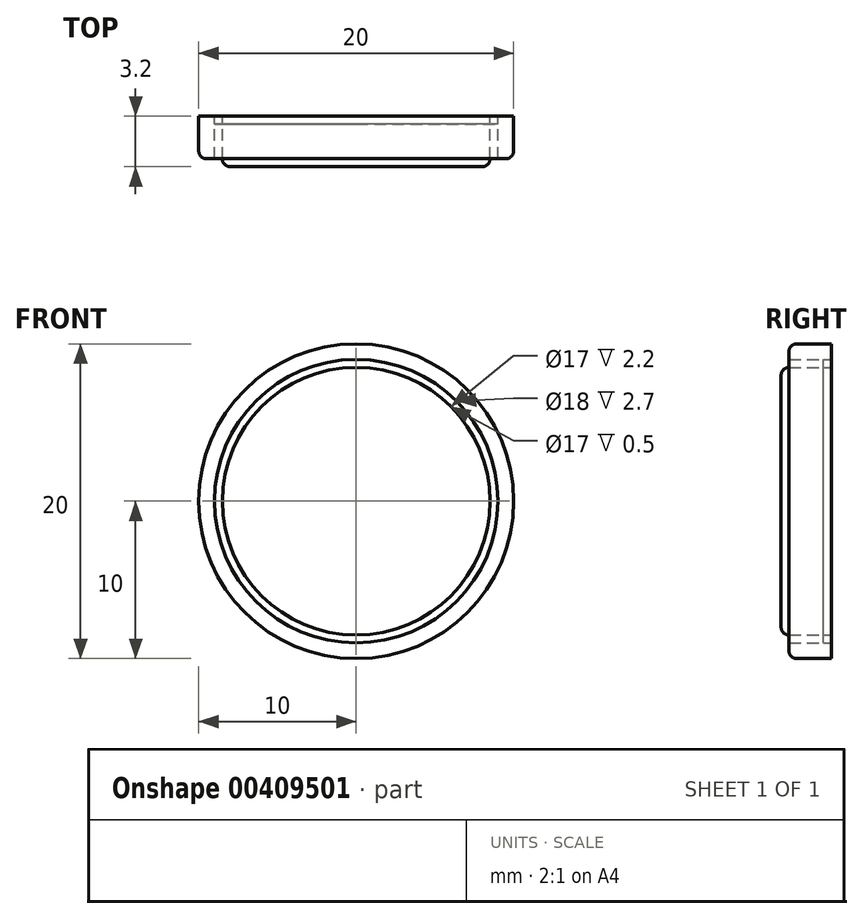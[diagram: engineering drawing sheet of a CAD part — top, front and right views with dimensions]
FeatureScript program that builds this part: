
annotation { "Feature Type Name" : "Feature", "Feature Type Description" : "" }
export const myFeature = defineFeature(function(context is Context, id is Id, definition is map)
    precondition{}
    {
        {
            var Q0;
            Q0=qCreatedBy(makeId("Front.planeOp"),FACE);
            var sketch = newSketch(context, id + "F0", { "sketchPlane" : qUnion([Q0]), "disableImprinting" : false});
            skCircle(sketch, "E0", {"center": v(0, 0) * mm, "radius": 10 * mm});
            skCircle(sketch, "E1", {"center": v(0, 0) * mm, "radius": 9 * mm});
            skCircle(sketch, "E2", {"center": v(0, 0) * mm, "radius": 8.5 * mm});
            skSolve(sketch);
        }
        {
            var Q0;
            Q0=makeQuery(id+"F0.imprint","IMPRINT",FACE,{"disambiguationData":[TD([[makeQuery(id+"F0.imprint","IMPRINT",EDGE,{"derivedFrom":sQuery(id+"F0.wireOp",EDGE,"E2")}),1.0]])]});
            var Q1;
            Q1=makeQuery(id+"F0.imprint","IMPRINT",FACE,{"disambiguationData":[TD([[makeQuery(id+"F0.imprint","IMPRINT",EDGE,{"derivedFrom":sQuery(id+"F0.wireOp",EDGE,"ab74bbfd-845b-4cb0-a3af-8f8529850c50.sketch_text.stroke-114")}),1.0]])]});
            var Q2;
            Q2=makeQuery(id+"F0.imprint","IMPRINT",FACE,{"disambiguationData":[TD([[makeQuery(id+"F0.imprint","IMPRINT",EDGE,{"derivedFrom":sQuery(id+"F0.wireOp",EDGE,"ab74bbfd-845b-4cb0-a3af-8f8529850c50.sketch_text.stroke-106")}),1.0]])]});
            var Q3;
            Q3=makeQuery(id+"F0.imprint","IMPRINT",FACE,{"disambiguationData":[TD([[makeQuery(id+"F0.imprint","IMPRINT",EDGE,{"derivedFrom":sQuery(id+"F0.wireOp",EDGE,"ab74bbfd-845b-4cb0-a3af-8f8529850c50.sketch_text.stroke-94")}),1.0]])]});
            var Q4;
            Q4=makeQuery(id+"F0.imprint","IMPRINT",FACE,{"disambiguationData":[TD([[makeQuery(id+"F0.imprint","IMPRINT",EDGE,{"derivedFrom":sQuery(id+"F0.wireOp",EDGE,"ab74bbfd-845b-4cb0-a3af-8f8529850c50.sketch_text.stroke-84")}),1.0]])]});
            var Q5;
            Q5=makeQuery(id+"F0.imprint","IMPRINT",FACE,{"disambiguationData":[TD([[makeQuery(id+"F0.imprint","IMPRINT",EDGE,{"derivedFrom":sQuery(id+"F0.wireOp",EDGE,"ab74bbfd-845b-4cb0-a3af-8f8529850c50.sketch_text.stroke-64")}),1.0]])]});
            var Q6;
            Q6=makeQuery(id+"F0.imprint","IMPRINT",FACE,{"disambiguationData":[TD([[makeQuery(id+"F0.imprint","IMPRINT",EDGE,{"derivedFrom":sQuery(id+"F0.wireOp",EDGE,"ab74bbfd-845b-4cb0-a3af-8f8529850c50.sketch_text.stroke-51")}),1.0]])]});
            var Q7;
            Q7=makeQuery(id+"F0.imprint","IMPRINT",FACE,{"disambiguationData":[TD([[makeQuery(id+"F0.imprint","IMPRINT",EDGE,{"derivedFrom":sQuery(id+"F0.wireOp",EDGE,"ab74bbfd-845b-4cb0-a3af-8f8529850c50.sketch_text.stroke-47")}),1.0]])]});
            var Q8;
            Q8=makeQuery(id+"F0.imprint","IMPRINT",FACE,{"disambiguationData":[TD([[makeQuery(id+"F0.imprint","IMPRINT",EDGE,{"derivedFrom":sQuery(id+"F0.wireOp",EDGE,"ab74bbfd-845b-4cb0-a3af-8f8529850c50.sketch_text.stroke-103")}),-1.0]])]});
            var Q9;
            Q9=makeQuery(id+"F0.imprint","IMPRINT",FACE,{"disambiguationData":[TD([[makeQuery(id+"F0.imprint","IMPRINT",EDGE,{"derivedFrom":sQuery(id+"F0.wireOp",EDGE,"ab74bbfd-845b-4cb0-a3af-8f8529850c50.sketch_text.stroke-43")}),1.0]])]});
            var Q10;
            Q10=makeQuery(id+"F0.imprint","IMPRINT",FACE,{"disambiguationData":[TD([[makeQuery(id+"F0.imprint","IMPRINT",EDGE,{"derivedFrom":sQuery(id+"F0.wireOp",EDGE,"ab74bbfd-845b-4cb0-a3af-8f8529850c50.sketch_text.stroke-30")}),1.0]])]});
            var Q11;
            Q11=makeQuery(id+"F0.imprint","IMPRINT",FACE,{"disambiguationData":[TD([[makeQuery(id+"F0.imprint","IMPRINT",EDGE,{"derivedFrom":sQuery(id+"F0.wireOp",EDGE,"ab74bbfd-845b-4cb0-a3af-8f8529850c50.sketch_text.stroke-14")}),1.0]])]});
            var Q12;
            Q12=makeQuery(id+"F0.imprint","IMPRINT",FACE,{"disambiguationData":[TD([[makeQuery(id+"F0.imprint","IMPRINT",EDGE,{"derivedFrom":sQuery(id+"F0.wireOp",EDGE,"ab74bbfd-845b-4cb0-a3af-8f8529850c50.sketch_text.stroke-6")}),1.0]])]});
            var Q13;
            Q13=makeQuery(id+"F0.imprint","IMPRINT",FACE,{"disambiguationData":[TD([[makeQuery(id+"F0.imprint","IMPRINT",EDGE,{"derivedFrom":sQuery(id+"F0.wireOp",EDGE,"ab74bbfd-845b-4cb0-a3af-8f8529850c50.sketch_text.stroke-10")}),1.0]])]});
            var Q14;
            Q14=makeQuery(id+"F0.imprint","IMPRINT",FACE,{"disambiguationData":[TD([[makeQuery(id+"F0.imprint","IMPRINT",EDGE,{"derivedFrom":sQuery(id+"F0.wireOp",EDGE,"ab74bbfd-845b-4cb0-a3af-8f8529850c50.sketch_text.stroke-0")}),1.0]])]});
            var Q15;
            Q15=makeQuery(id+"F0.imprint","IMPRINT",FACE,{"disambiguationData":[TD([[makeQuery(id+"F0.imprint","IMPRINT",EDGE,{"derivedFrom":sQuery(id+"F0.wireOp",EDGE,"ab74bbfd-845b-4cb0-a3af-8f8529850c50.sketch_text.stroke-183")}),1.0]])]});
            var Q16;
            Q16=makeQuery(id+"F0.imprint","IMPRINT",FACE,{"disambiguationData":[TD([[makeQuery(id+"F0.imprint","IMPRINT",EDGE,{"derivedFrom":sQuery(id+"F0.wireOp",EDGE,"ab74bbfd-845b-4cb0-a3af-8f8529850c50.sketch_text.stroke-167")}),1.0]])]});
            var Q17;
            Q17=makeQuery(id+"F0.imprint","IMPRINT",FACE,{"disambiguationData":[TD([[makeQuery(id+"F0.imprint","IMPRINT",EDGE,{"derivedFrom":sQuery(id+"F0.wireOp",EDGE,"ab74bbfd-845b-4cb0-a3af-8f8529850c50.sketch_text.stroke-159")}),1.0]])]});
            var Q18;
            Q18=makeQuery(id+"F0.imprint","IMPRINT",FACE,{"disambiguationData":[TD([[makeQuery(id+"F0.imprint","IMPRINT",EDGE,{"derivedFrom":sQuery(id+"F0.wireOp",EDGE,"ab74bbfd-845b-4cb0-a3af-8f8529850c50.sketch_text.stroke-163")}),-1.0]])]});
            var Q19;
            Q19=makeQuery(id+"F0.imprint","IMPRINT",FACE,{"disambiguationData":[TD([[makeQuery(id+"F0.imprint","IMPRINT",EDGE,{"derivedFrom":sQuery(id+"F0.wireOp",EDGE,"ab74bbfd-845b-4cb0-a3af-8f8529850c50.sketch_text.stroke-147")}),1.0]])]});
            var Q20;
            Q20=makeQuery(id+"F0.imprint","IMPRINT",FACE,{"disambiguationData":[TD([[makeQuery(id+"F0.imprint","IMPRINT",EDGE,{"derivedFrom":sQuery(id+"F0.wireOp",EDGE,"ab74bbfd-845b-4cb0-a3af-8f8529850c50.sketch_text.stroke-132")}),-1.0]])]});
            var Q21;
            Q21=makeQuery(id+"F0.imprint","IMPRINT",FACE,{"disambiguationData":[TD([[makeQuery(id+"F0.imprint","IMPRINT",EDGE,{"derivedFrom":sQuery(id+"F0.wireOp",EDGE,"ab74bbfd-845b-4cb0-a3af-8f8529850c50.sketch_text.stroke-132")}),1.0]])]});
            var Q22;
            Q22=makeQuery(id+"F0.imprint","IMPRINT",FACE,{"disambiguationData":[TD([[makeQuery(id+"F0.imprint","IMPRINT",EDGE,{"derivedFrom":sQuery(id+"F0.wireOp",EDGE,"ab74bbfd-845b-4cb0-a3af-8f8529850c50.sketch_text.stroke-122")}),1.0]])]});
            var Q23;
            Q23=makeQuery(id+"F0.imprint","IMPRINT",FACE,{"disambiguationData":[TD([[makeQuery(id+"F0.imprint","IMPRINT",EDGE,{"derivedFrom":sQuery(id+"F0.wireOp",EDGE,"ab74bbfd-845b-4cb0-a3af-8f8529850c50.sketch_text.stroke-211")}),1.0]])]});
            var Q24;
            Q24=makeQuery(id+"F0.imprint","IMPRINT",FACE,{"disambiguationData":[TD([[makeQuery(id+"F0.imprint","IMPRINT",EDGE,{"derivedFrom":sQuery(id+"F0.wireOp",EDGE,"ab74bbfd-845b-4cb0-a3af-8f8529850c50.sketch_text.stroke-195")}),1.0]])]});
            extrude(context, id + "F1", {"entities" : qUnion([Q0, Q1, Q2, Q3, Q4, Q5, Q6, Q7, Q8, Q9, Q10, Q11, Q12, Q13, Q14, Q15, Q16, Q17, Q18, Q19, Q20, Q21, Q22, Q23, Q24]), "depth" : 3.2 * mm});
        }
        {
            var Q0;
            Q0=makeQuery(id+"F0.imprint","IMPRINT",FACE,{"disambiguationData":[TD([[makeQuery(id+"F0.imprint","IMPRINT",EDGE,{"derivedFrom":sQuery(id+"F0.wireOp",EDGE,"E1")}),1.0]])]});
            extrude(context, id + "F2", {"entities" : qUnion([Q0]), "depth" : 2.2 * mm});
        }
        {
            var Q0;
            Q0=makeQuery(id+"F0.imprint","IMPRINT",FACE,{"disambiguationData":[TD([[makeQuery(id+"F0.imprint","IMPRINT",EDGE,{"derivedFrom":sQuery(id+"F0.wireOp",EDGE,"E0")}),1.0]])]});
            extrude(context, id + "F3", {"entities" : qUnion([Q0]), "depth" : 2.7 * mm});
        }
        {
            var Q0;
            Q0=makeQuery(id+"F3.opExtrude","CAP_EDGE",EDGE,{"disambiguationData":[OSD([sQuery(id+"F0.wireOp",EDGE,"E0")])],"isStart":false});
            fillet(context, id + "F4", {"entities" : qUnion([Q0]), "radius" : 0.5 * mm, "tangentPropagation" : true, "allowEdgeOverflow" : false});
        }
        {
            var Q0;
            Q0=makeQuery(id+"F1.opExtrude","CAP_EDGE",EDGE,{"disambiguationData":[OSD([sQuery(id+"F0.wireOp",EDGE,"E2")])],"isStart":false});
            fillet(context, id + "F5", {"entities" : qUnion([Q0]), "radius" : 0.5 * mm, "tangentPropagation" : true, "allowEdgeOverflow" : false});
        }
        {
            var Q0;
            Q0=makeQuery(id+"F2.opExtrude","SWEPT_BODY",BODY,{"disambiguationData":[OSD([sQuery(id+"F0.wireOp",EDGE,"E1"),sQuery(id+"F0.wireOp",EDGE,"E2")])]});
            transform(context, id + "F6", {"entities" : qUnion([Q0]), "transformType" : TransformType.TRANSLATION_3D, "dx" : 0 * mm, "dy" : -0.5 * mm, "dz" : 0 * mm, "makeCopy" : false});
        }
        {
            var Q0;
            Q0=makeQuery(id+"F3.opExtrude","CAP_FACE",FACE,{"disambiguationData":[OSD([sQuery(id+"F0.wireOp",EDGE,"E0"),sQuery(id+"F0.wireOp",EDGE,"E1")])],"isStart":false});
            extrude(context, id + "F7", {"entities" : qUnion([Q0]), "depth" : 0.5 * mm});
        }
        {
            var Q0;
            Q0=makeQuery(id+"F7.opExtrude","SWEPT_BODY",BODY,{"disambiguationData":[OSD([sQuery(id+"F0.wireOp",EDGE,"E0"),sQuery(id+"F0.wireOp",EDGE,"E1")])]});
            deleteBodies(context, id + "F8", {"entities" : qUnion([Q0])});
        }
        {
            var Q0;
            Q0=makeQuery(id+"F0.imprint","IMPRINT",FACE,{"disambiguationData":[TD([[makeQuery(id+"F0.imprint","IMPRINT",EDGE,{"derivedFrom":sQuery(id+"F0.wireOp",EDGE,"E1")}),1.0]])]});
            var Q1;
            Q1=sQuery(id+"F0.wireOp",EDGE,"E1");
            extrude(context, id + "F9", {"entities" : qUnion([Q0]), "surfaceEntities" : qUnion([Q1]), "depth" : 0.5 * mm});
        }
    });
